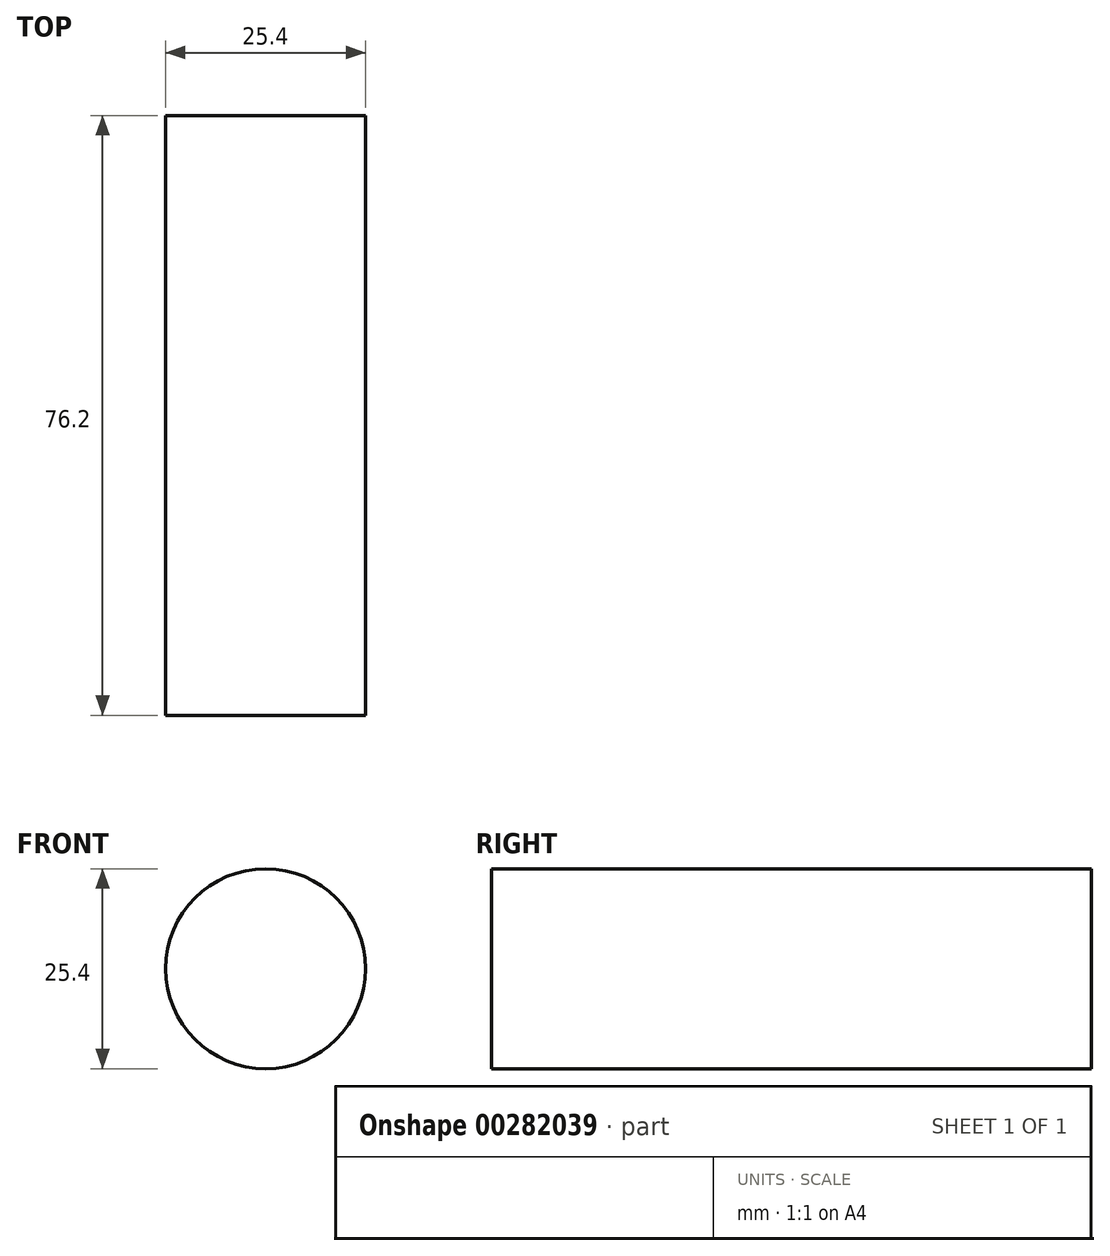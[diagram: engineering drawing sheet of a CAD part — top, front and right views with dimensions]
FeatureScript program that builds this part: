
annotation { "Feature Type Name" : "Feature", "Feature Type Description" : "" }
export const myFeature = defineFeature(function(context is Context, id is Id, definition is map)
    precondition{}
    {
        {
            var Q0;
            Q0=qCreatedBy(makeId("Front.planeOp"),FACE);
            var sketch = newSketch(context, id + "F0", { "sketchPlane" : qUnion([Q0])});
            skCircle(sketch, "E0", {"center": v(-39.15, 41.44) * mm, "radius": 12.7 * mm});
            skSolve(sketch);
        }
        {
            var Q0;
            Q0 = qSketchRegion(id + "F0", true);
            extrude(context, id + "F1", {"entities" : qUnion([Q0]), "depth" : 76.2 * mm});
        }
    });
